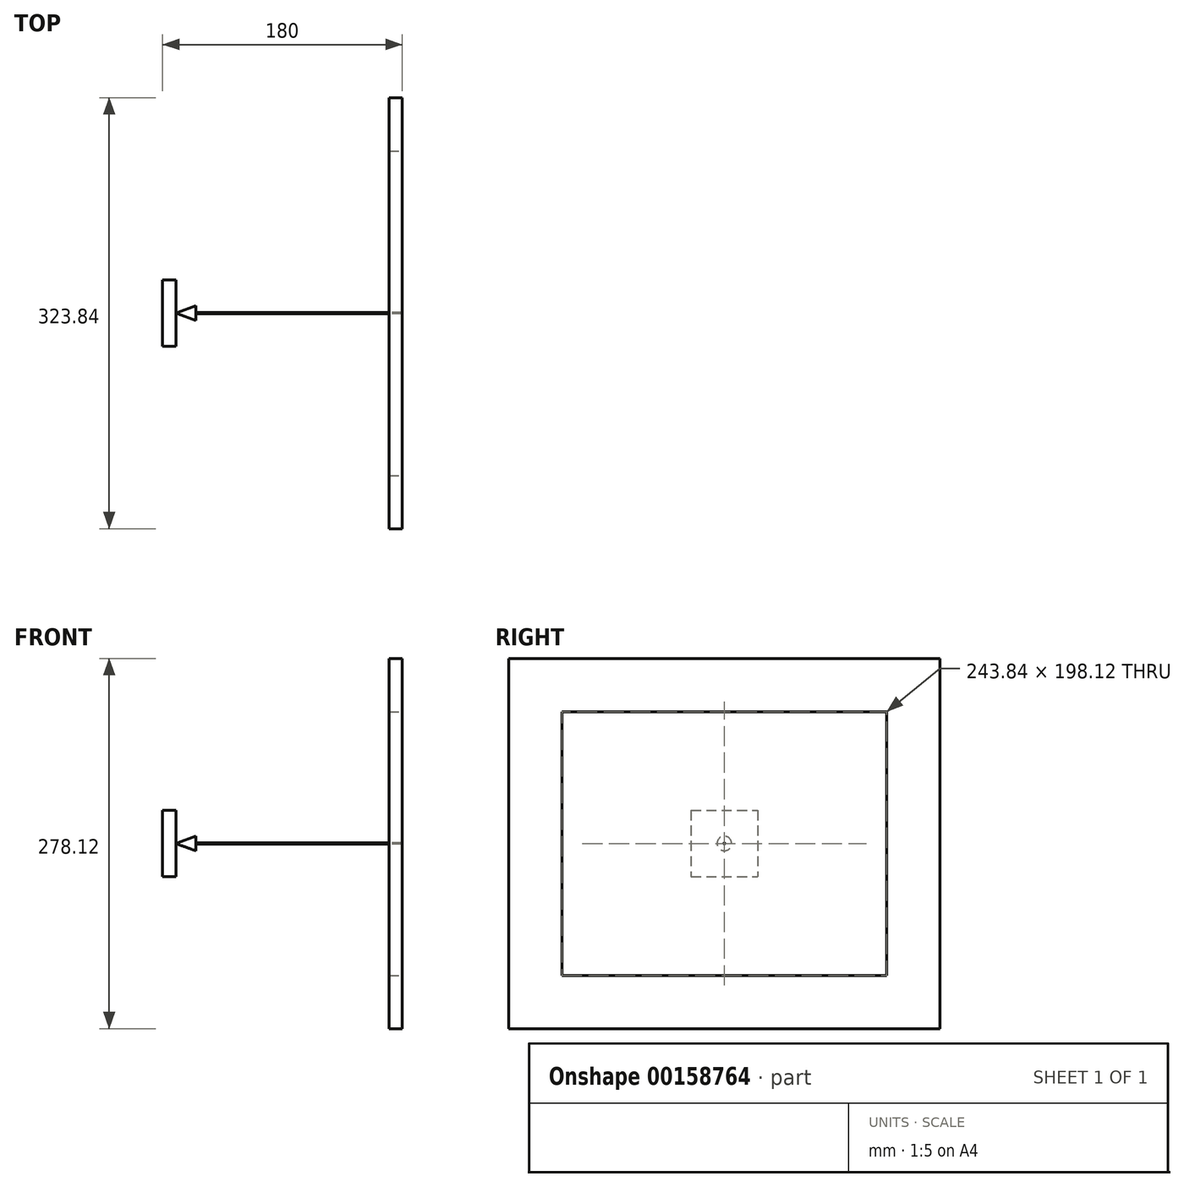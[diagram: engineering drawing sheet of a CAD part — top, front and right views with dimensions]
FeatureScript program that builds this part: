
annotation { "Feature Type Name" : "Feature", "Feature Type Description" : "" }
export const myFeature = defineFeature(function(context is Context, id is Id, definition is map)
    precondition{}
    {
        {
            var Q0;
            Q0=qCreatedBy(makeId("Top.planeOp"),FACE);
            var sketch = newSketch(context, id + "F0", { "sketchPlane" : qUnion([Q0])});
            skLineSegment(sketch, "E0.rect.bottom", {"start": v(-350, 350) * mm, "end": v(350, 350) * mm});
            skLineSegment(sketch, "E0.rect.top", {"start": v(-350, -350) * mm, "end": v(350, -350) * mm});
            skLineSegment(sketch, "E0.rect.left", {"start": v(-350, 350) * mm, "end": v(-350, -350) * mm});
            skLineSegment(sketch, "E0.rect.right", {"start": v(350, 350) * mm, "end": v(350, -350) * mm});
            skPoint(sketch, "E0.rect.middle", {"position": v(0, 0) * mm});
            skSolve(sketch);
        }
        {
            var Q0;
            Q0=makeQuery(id+"F0.imprint","IMPRINT",FACE,{"disambiguationData":[TD([[makeQuery(id+"F0.imprint","IMPRINT",EDGE,{"derivedFrom":sQuery(id+"F0.wireOp",EDGE,"E0.rect.bottom")}),-1.0]])]});
            extrude(context, id + "F1", {"entities" : qUnion([Q0]), "oppositeDirection" : true, "depth" : 70 * mm});
        }
        {
            var Q0;
            Q0=makeQuery(id+"F1.opExtrude","CAP_FACE",FACE,{"disambiguationData":[OSD([sQuery(id+"F0.wireOp",EDGE,"E0.rect.bottom"),sQuery(id+"F0.wireOp",EDGE,"E0.rect.top"),sQuery(id+"F0.wireOp",EDGE,"E0.rect.left"),sQuery(id+"F0.wireOp",EDGE,"E0.rect.right")])],"isStart":true});
            var sketch = newSketch(context, id + "F2", { "sketchPlane" : qUnion([Q0])});
            skCircle(sketch, "E1", {"center": v(0, 0) * mm, "radius": 285.19 * mm});
            skSolve(sketch);
        }
        {
            var Q0;
            Q0=makeQuery(id+"F2.imprint","IMPRINT",FACE,{"disambiguationData":[TD([[makeQuery(id+"F2.imprint","IMPRINT",EDGE,{"derivedFrom":sQuery(id+"F2.wireOp",EDGE,"E1")}),1.0]])]});
            extrude(context, id + "F3", {"entities" : qUnion([Q0]), "operationType" : NewBodyOperationType.ADD, "depth" : 10 * mm});
        }
        {
            var Q0;
            Q0=makeQuery(id+"F3.opExtrude","CAP_FACE",FACE,{"disambiguationData":[OSD([sQuery(id+"F2.wireOp",EDGE,"E1")])],"isStart":false});
            var sketch = newSketch(context, id + "F4", { "sketchPlane" : qUnion([Q0])});
            skCircle(sketch, "E2", {"center": v(0, 0) * mm, "radius": 219.2 * mm});
            skSolve(sketch);
        }
        {
            var Q0;
            Q0=makeQuery(id+"F4.imprint","IMPRINT",FACE,{"disambiguationData":[TD([[makeQuery(id+"F4.imprint","IMPRINT",EDGE,{"derivedFrom":sQuery(id+"F4.wireOp",EDGE,"E2")}),1.0]])]});
            extrude(context, id + "F5", {"entities" : qUnion([Q0]), "operationType" : NewBodyOperationType.ADD, "depth" : 25 * mm});
        }
        {
            var Q0;
            Q0=makeQuery(id+"F5.opExtrude","CAP_FACE",FACE,{"disambiguationData":[OSD([sQuery(id+"F4.wireOp",EDGE,"E2")])],"isStart":false});
            var sketch = newSketch(context, id + "F6", { "sketchPlane" : qUnion([Q0])});
            skCircle(sketch, "E3", {"center": v(0, 0) * mm, "radius": 146.56 * mm});
            skSolve(sketch);
        }
        {
            var Q0;
            Q0=makeQuery(id+"F6.imprint","IMPRINT",FACE,{"disambiguationData":[TD([[makeQuery(id+"F6.imprint","IMPRINT",EDGE,{"derivedFrom":sQuery(id+"F6.wireOp",EDGE,"E3")}),1.0]])]});
            extrude(context, id + "F7", {"entities" : qUnion([Q0]), "operationType" : NewBodyOperationType.ADD, "depth" : 25 * mm});
        }
        {
            var Q0;
            Q0=qCreatedBy(makeId("Right.planeOp"),FACE);
            cPlane(context, id + "F8", {"entities" : qUnion([Q0]), "cplaneType" : CPlaneType.OFFSET, "offset" : 250 * mm, "oppositeDirection" : true, "width" : 150 * mm, "height" : 150 * mm});
        }
        {
            var Q0;
            Q0=qCreatedBy(id+"F8.planeOp",FACE);
            var sketch = newSketch(context, id + "F9", { "sketchPlane" : qUnion([Q0])});
            skLineSegment(sketch, "E4.rect.bottom", {"start": v(-25, 325) * mm, "end": v(25, 325) * mm});
            skLineSegment(sketch, "E4.rect.top", {"start": v(-25, 275) * mm, "end": v(25, 275) * mm});
            skLineSegment(sketch, "E4.rect.left", {"start": v(-25, 325) * mm, "end": v(-25, 275) * mm});
            skLineSegment(sketch, "E4.rect.right", {"start": v(25, 325) * mm, "end": v(25, 275) * mm});
            skPoint(sketch, "E4.rect.middle", {"position": v(0, 300) * mm});
            skSolve(sketch);
        }
        {
            var Q0;
            Q0=makeQuery(id+"F9.imprint","IMPRINT",FACE,{"disambiguationData":[TD([[makeQuery(id+"F9.imprint","IMPRINT",EDGE,{"derivedFrom":sQuery(id+"F9.wireOp",EDGE,"E4.rect.bottom")}),-1.0]])]});
            extrude(context, id + "F10", {"entities" : qUnion([Q0]), "oppositeDirection" : true, "depth" : 10 * mm});
        }
        {
            var Q0;
            Q0=makeQuery(id+"F10.opExtrude","CAP_FACE",FACE,{"disambiguationData":[OSD([sQuery(id+"F9.wireOp",EDGE,"E4.rect.bottom"),sQuery(id+"F9.wireOp",EDGE,"E4.rect.top"),sQuery(id+"F9.wireOp",EDGE,"E4.rect.left"),sQuery(id+"F9.wireOp",EDGE,"E4.rect.right")])],"isStart":true});
            var sketch = newSketch(context, id + "F11", { "sketchPlane" : qUnion([Q0])});
            skCircle(sketch, "E5", {"center": v(0, 300) * mm, "radius": 0.5 * mm});
            skSolve(sketch);
        }
        {
            var Q0;
            Q0=makeQuery(id+"F11.imprint","IMPRINT",FACE,{"disambiguationData":[TD([[makeQuery(id+"F11.imprint","IMPRINT",EDGE,{"derivedFrom":sQuery(id+"F11.wireOp",EDGE,"E5")}),1.0]])]});
            extrude(context, id + "F12", {"entities" : qUnion([Q0]), "operationType" : NewBodyOperationType.ADD, "depth" : 160 * mm});
        }
        {
            var Q0;
            Q0=makeQuery(id+"F7.opExtrude","CAP_EDGE",EDGE,{"disambiguationData":[OSD([sQuery(id+"F6.wireOp",EDGE,"E3")])],"isStart":false});
            var Q1;
            Q1=makeQuery(id+"F5.opExtrude","CAP_EDGE",EDGE,{"disambiguationData":[OSD([sQuery(id+"F4.wireOp",EDGE,"E2")])],"isStart":false});
            var Q2;
            Q2=makeQuery(id+"F3.opExtrude","CAP_EDGE",EDGE,{"disambiguationData":[OSD([sQuery(id+"F2.wireOp",EDGE,"E1")])],"isStart":false});
            chamfer(context, id + "F13", {"entities" : qUnion([Q0, Q1, Q2]), "width" : 5 * mm, "tangentPropagation" : true});
        }
        {
            var Q0;
            Q0=makeQuery(id+"F1.opExtrude","CAP_EDGE",EDGE,{"disambiguationData":[OSD([sQuery(id+"F0.wireOp",EDGE,"E0.rect.top")])],"isStart":true});
            var Q1;
            Q1=makeQuery(id+"F1.opExtrude","CAP_FACE",FACE,{"disambiguationData":[OSD([sQuery(id+"F0.wireOp",EDGE,"E0.rect.bottom"),sQuery(id+"F0.wireOp",EDGE,"E0.rect.top"),sQuery(id+"F0.wireOp",EDGE,"E0.rect.left"),sQuery(id+"F0.wireOp",EDGE,"E0.rect.right")])],"isStart":true});
            fillet(context, id + "F14", {"entities" : qUnion([Q0, Q1]), "radius" : 2 * mm, "tangentPropagation" : true, "allowEdgeOverflow" : false});
        }
        {
            var Q0;
            Q0=qCreatedBy(makeId("Front.planeOp"),FACE);
            var sketch = newSketch(context, id + "F15", { "sketchPlane" : qUnion([Q0])});
            skLineSegment(sketch, "E6", {"start": v(-250, 300) * mm, "end": v(-235, 305.46) * mm});
            skLineSegment(sketch, "E7", {"start": v(-235, 305.46) * mm, "end": v(-235, 300) * mm});
            skLineSegment(sketch, "E8", {"start": v(-235, 300) * mm, "end": v(-250, 300) * mm});
            skSolve(sketch);
        }
        {
            var Q0;
            Q0=makeQuery(id+"F15.imprint","IMPRINT",FACE,{"disambiguationData":[TD([[makeQuery(id+"F15.imprint","IMPRINT",EDGE,{"derivedFrom":sQuery(id+"F15.wireOp",EDGE,"E6")}),-1.0]])]});
            var Q1;
            Q1=sQuery(id+"F15.wireOp",EDGE,"E8");
            revolve(context, id + "F16", {"operationType" : NewBodyOperationType.ADD, "entities" : qUnion([Q0]), "axis" : qUnion([Q1]), "revolveType" : RevolveType.FULL});
        }
        {
            var Q0;
            Q0=makeQuery(id+"F1.opExtrude","SWEPT_BODY",BODY,{"disambiguationData":[OSD([sQuery(id+"F0.wireOp",EDGE,"E0.rect.bottom"),sQuery(id+"F0.wireOp",EDGE,"E0.rect.top"),sQuery(id+"F0.wireOp",EDGE,"E0.rect.left"),sQuery(id+"F0.wireOp",EDGE,"E0.rect.right")])]});
            deleteBodies(context, id + "F17", {"entities" : qUnion([Q0])});
        }
        {
            var Q0;
            Q0=makeQuery(id+"F12.opExtrude","CAP_FACE",FACE,{"disambiguationData":[OSD([sQuery(id+"F11.wireOp",EDGE,"E5")])],"isStart":false});
            var sketch = newSketch(context, id + "F18", { "sketchPlane" : qUnion([Q0])});
            skLineSegment(sketch, "E9.bottom", {"start": v(-121.92, 399.06) * mm, "end": v(121.92, 399.06) * mm});
            skLineSegment(sketch, "E9.top", {"start": v(-121.92, 200.94) * mm, "end": v(121.92, 200.94) * mm});
            skLineSegment(sketch, "E9.left", {"start": v(-121.92, 399.06) * mm, "end": v(-121.92, 200.94) * mm});
            skLineSegment(sketch, "E9.right", {"start": v(121.92, 399.06) * mm, "end": v(121.92, 200.94) * mm});
            skLineSegment(sketch, "E10", {"start": v(-121.92, 399.06) * mm, "end": v(121.92, 200.94) * mm, "construction": true});
            skLineSegment(sketch, "E11", {"start": v(121.92, 399.06) * mm, "end": v(-121.92, 200.94) * mm, "construction": true});
            skPoint(sketch, "E12", {"position": v(0, 300) * mm});
            skSolve(sketch);
        }
        {
            var Q0;
            Q0=makeQuery(id+"F18.imprint","IMPRINT",FACE,{"disambiguationData":[TD([[makeQuery(id+"F18.imprint","IMPRINT",EDGE,{"derivedFrom":sQuery(id+"F18.wireOp",EDGE,"E9.bottom")}),-1.0]])]});
            extrude(context, id + "F19", {"entities" : qUnion([Q0]), "depth" : 10 * mm});
        }
        {
            var Q0;
            Q0=makeQuery(id+"F19.opExtrude","CAP_FACE",FACE,{"disambiguationData":[OSD([sQuery(id+"F11.wireOp",EDGE,"E5"),sQuery(id+"F18.wireOp",EDGE,"E9.bottom"),sQuery(id+"F18.wireOp",EDGE,"E9.top"),sQuery(id+"F18.wireOp",EDGE,"E9.left"),sQuery(id+"F18.wireOp",EDGE,"E9.right")])],"isStart":false});
            var sketch = newSketch(context, id + "F20", { "sketchPlane" : qUnion([Q0])});
            skLineSegment(sketch, "E13.bottom", {"start": v(-161.92, 439.06) * mm, "end": v(161.92, 439.06) * mm});
            skLineSegment(sketch, "E13.top", {"start": v(-161.92, 160.94) * mm, "end": v(161.92, 160.94) * mm});
            skLineSegment(sketch, "E13.left", {"start": v(-161.92, 439.06) * mm, "end": v(-161.92, 160.94) * mm});
            skLineSegment(sketch, "E13.right", {"start": v(161.92, 439.06) * mm, "end": v(161.92, 160.94) * mm});
            skLineSegment(sketch, "E14", {"start": v(-161.92, 439.06) * mm, "end": v(161.92, 160.94) * mm, "construction": true});
            skLineSegment(sketch, "E15", {"start": v(161.92, 439.06) * mm, "end": v(-161.92, 160.94) * mm, "construction": true});
            skPoint(sketch, "E16", {"position": v(0, 300) * mm});
            skSolve(sketch);
        }
        {
            var Q0;
            Q0=makeQuery(id+"F20.imprint","IMPRINT",FACE,{"disambiguationData":[TD([[makeQuery(id+"F20.imprint","IMPRINT",EDGE,{"derivedFrom":sQuery(id+"F20.wireOp",EDGE,"E13.bottom")}),-1.0]])]});
            var Q1;
            Q1=makeQuery(id+"F19.opExtrude","CAP_FACE",FACE,{"disambiguationData":[OSD([sQuery(id+"F11.wireOp",EDGE,"E5"),sQuery(id+"F18.wireOp",EDGE,"E9.bottom"),sQuery(id+"F18.wireOp",EDGE,"E9.top"),sQuery(id+"F18.wireOp",EDGE,"E9.left"),sQuery(id+"F18.wireOp",EDGE,"E9.right")])],"isStart":true});
            extrude(context, id + "F21", {"entities" : qUnion([Q0]), "endBound" : BoundingType.UP_TO_SURFACE, "oppositeDirection" : true, "endBoundEntityFace" : qUnion([Q1]), "depth" : 25 * mm});
        }
    });
